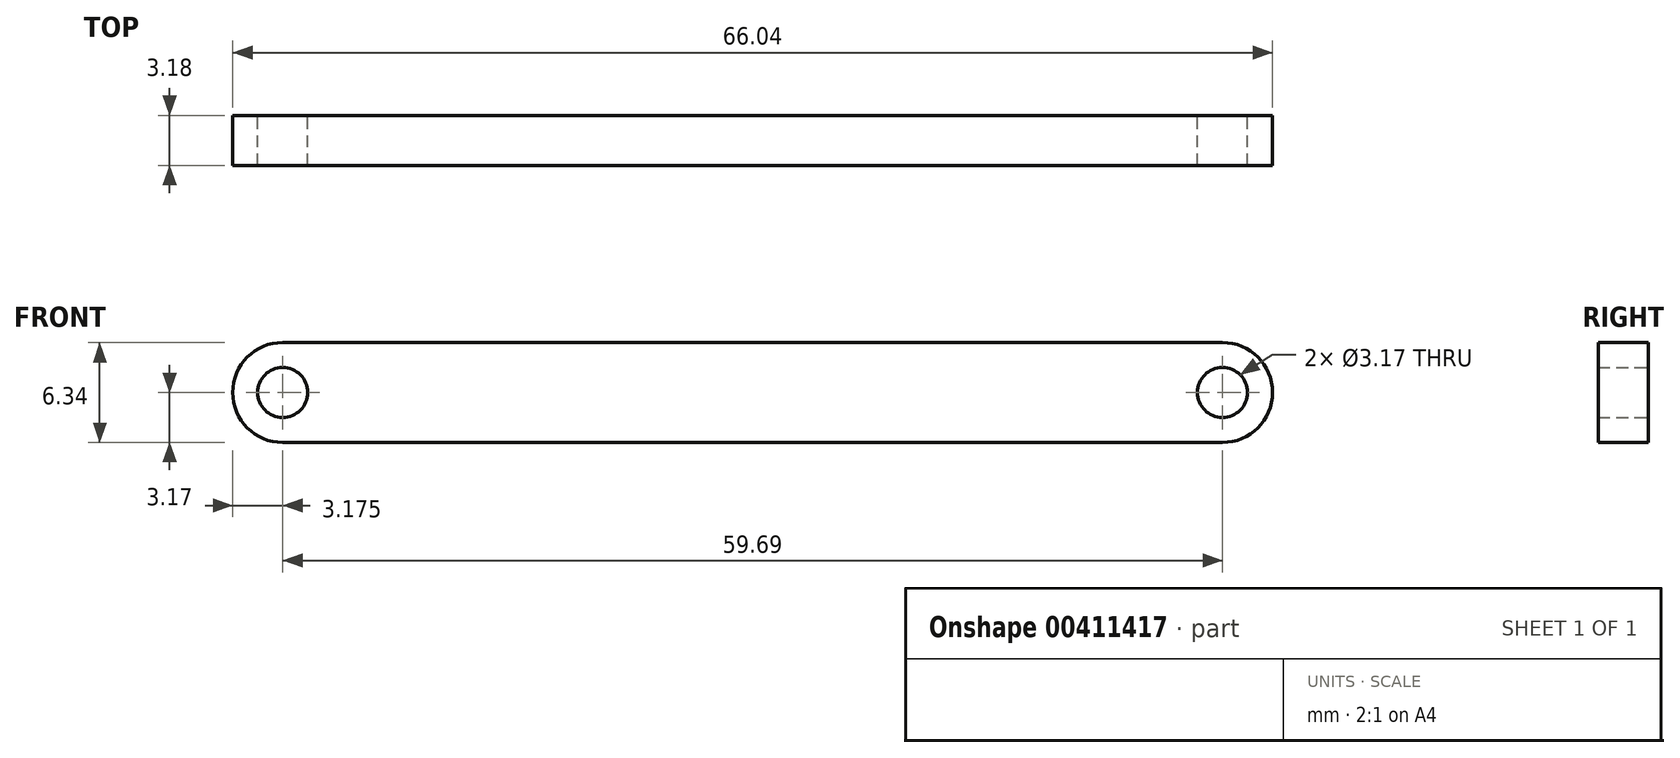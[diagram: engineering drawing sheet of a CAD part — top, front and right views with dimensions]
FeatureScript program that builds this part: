
annotation { "Feature Type Name" : "Feature", "Feature Type Description" : "" }
export const myFeature = defineFeature(function(context is Context, id is Id, definition is map)
    precondition{}
    {
        {
            var Q0;
            Q0=qCreatedBy(makeId("Front.planeOp"),FACE);
            var sketch = newSketch(context, id + "F0", { "sketchPlane" : qUnion([Q0])});
            skArc(sketch, "E0", {"start": v(29.84, -3.18) * mm, "mid": v(33.02, 0) * mm, "end": v(29.84, 3.18) * mm});
            skArc(sketch, "E1", {"start": v(-29.84, 3.18) * mm, "mid": v(-33.02, 0) * mm, "end": v(-29.84, -3.18) * mm});
            skLineSegment(sketch, "E2", {"start": v(-29.84, 3.18) * mm, "end": v(29.84, 3.18) * mm});
            skLineSegment(sketch, "E3", {"start": v(-29.85, -3.18) * mm, "end": v(29.84, -3.18) * mm});
            skCircle(sketch, "E4", {"center": v(-29.84, 0) * mm, "radius": 1.59 * mm});
            skCircle(sketch, "E5", {"center": v(29.84, 0) * mm, "radius": 1.59 * mm});
            skSolve(sketch);
        }
        {
            var Q0;
            Q0 = qSketchRegion(id + "F0", true);
            extrude(context, id + "F1", {"entities" : qUnion([Q0]), "depth" : 3.17 * mm});
        }
    });
